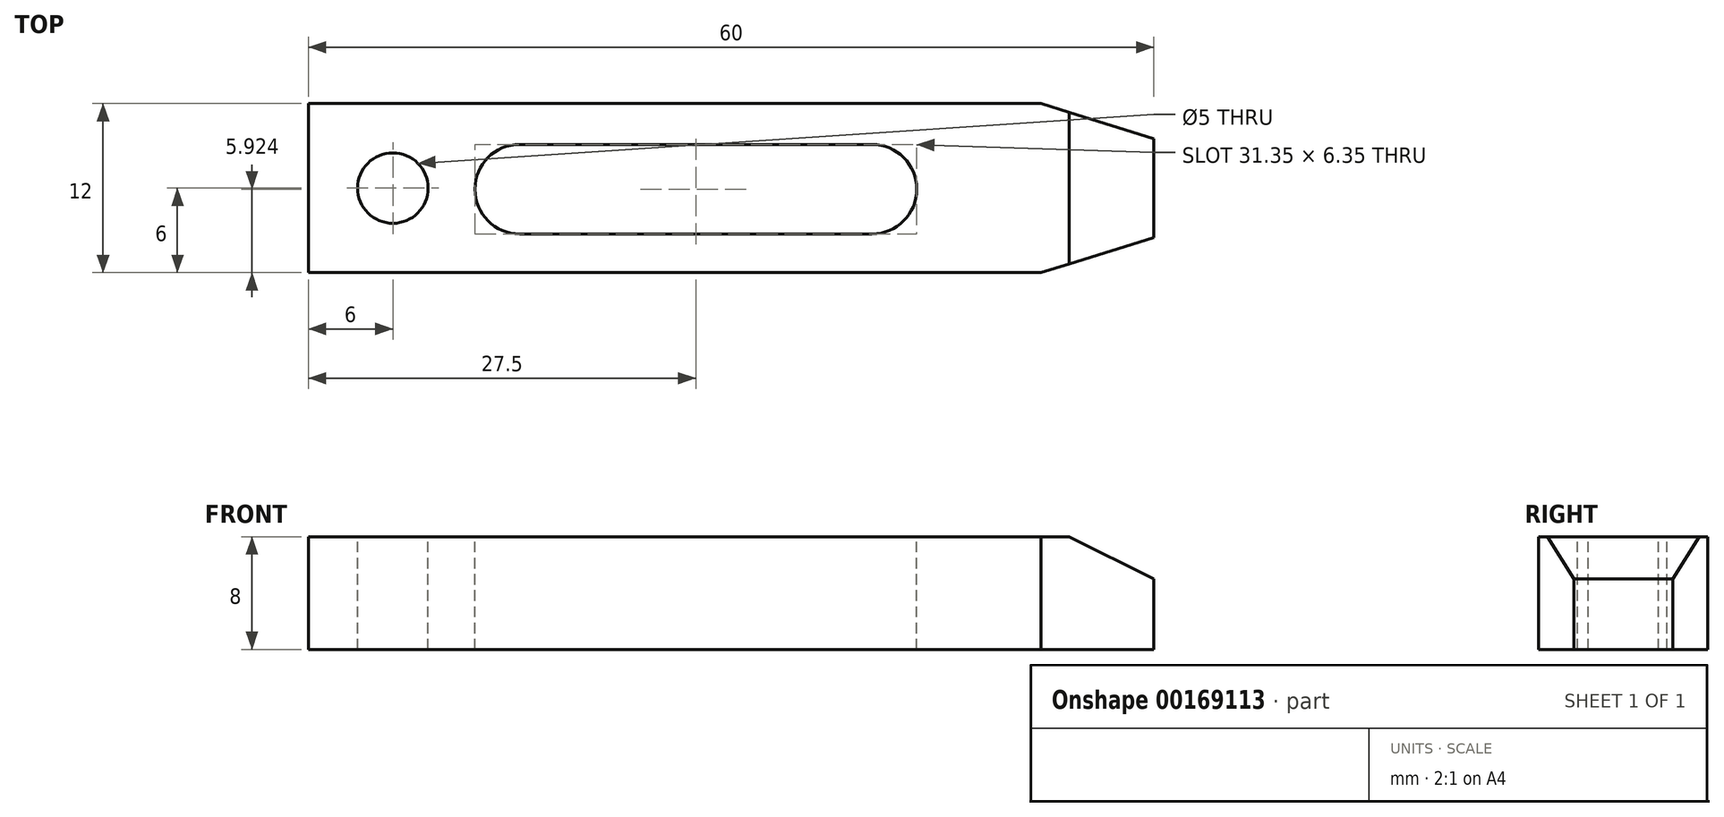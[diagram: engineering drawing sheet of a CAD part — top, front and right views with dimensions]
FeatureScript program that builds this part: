
annotation { "Feature Type Name" : "Feature", "Feature Type Description" : "" }
export const myFeature = defineFeature(function(context is Context, id is Id, definition is map)
    precondition{}
    {
        {
            var Q0;
            Q0=qCreatedBy(makeId("Top.planeOp"),FACE);
            var sketch = newSketch(context, id + "F0", { "sketchPlane" : qUnion([Q0])});
            skLineSegment(sketch, "E0.bottom", {"start": v(0, 0) * mm, "end": v(60, 0) * mm});
            skLineSegment(sketch, "E0.top", {"start": v(0, 12) * mm, "end": v(60, 12) * mm});
            skLineSegment(sketch, "E0.left", {"start": v(0, 0) * mm, "end": v(0, 12) * mm});
            skLineSegment(sketch, "E0.right", {"start": v(60, 0) * mm, "end": v(60, 12) * mm});
            skLineSegment(sketch, "E1", {"start": v(0, 6) * mm, "end": v(60, 6) * mm, "construction": true});
            skLineSegment(sketch, "E2", {"start": v(52, 12) * mm, "end": v(60, 9.5) * mm});
            skLineSegment(sketch, "E3.MirrorCS", {"start": v(52, 0) * mm, "end": v(60, 2.5) * mm});
            skSolve(sketch);
        }
        {
            var Q0;
            {var subQ3=sQuery(id+"F0.wireOp",EDGE,"E0.left");Q0=makeQuery(id+"F0.imprint","IMPRINT",FACE,{"disambiguationData":[TD([[makeQuery(id+"F0.imprint","IMPRINT",EDGE,{"derivedFrom":subQ3}),-1.0]])]});}
            extrude(context, id + "F1", {"entities" : qUnion([Q0]), "depth" : 8 * mm});
        }
        {
            var Q0;
            Q0=makeQuery(id+"F1.opExtrude","CAP_FACE",FACE,{"disambiguationData":[OSD([sQuery(id+"F0.wireOp",EDGE,"E0.bottom"),sQuery(id+"F0.wireOp",EDGE,"E0.top"),sQuery(id+"F0.wireOp",EDGE,"E0.left"),sQuery(id+"F0.wireOp",EDGE,"E0.right"),sQuery(id+"F0.wireOp",EDGE,"E2"),sQuery(id+"F0.wireOp",EDGE,"E3.MirrorCS")])],"isStart":false});
            var sketch = newSketch(context, id + "F2", { "sketchPlane" : qUnion([Q0])});
            skPoint(sketch, "E4", {"position": v(6, 6) * mm});
            skSolve(sketch);
        }
        {
            var Q0;
            Q0=sQuery(id+"F2.wireOp",VERTEX,"E4");
            var Q1;
            Q1=makeQuery(id+"F1.opExtrude","SWEPT_BODY",BODY,{"disambiguationData":[OSD([sQuery(id+"F0.wireOp",EDGE,"E0.bottom"),sQuery(id+"F0.wireOp",EDGE,"E0.top"),sQuery(id+"F0.wireOp",EDGE,"E0.left"),sQuery(id+"F0.wireOp",EDGE,"E0.right"),sQuery(id+"F0.wireOp",EDGE,"E2"),sQuery(id+"F0.wireOp",EDGE,"E3.MirrorCS")])]});
            hole(context, id + "F3", {"style" : HoleStyle.SIMPLE, "endStyle" : HoleEndStyle.THROUGH, "standardTappedOrClearance" : lookupTablePath({ "standard" : "ISO", "engagement" : "75%", "pitch" : "1 mm", "size" : "M6", "type" : "Tapped" }), "standardBlindInLast" : lookupTablePath({ "standard" : "ISO", "engagement" : "75%", "pitch" : "1 mm", "size" : "M6", "type" : "Tapped" }), "holeDiameter" : 5 * mm, "locations" : qUnion([Q0]), "scope" : qUnion([Q1]), "isTappedThrough" : true, "majorDiameter" : 6 * mm, "showTappedDepth" : true});
        }
        {
            var Q0;
            Q0=makeQuery(id+"F1.opExtrude","CAP_FACE",FACE,{"disambiguationData":[OSD([sQuery(id+"F0.wireOp",EDGE,"E0.bottom"),sQuery(id+"F0.wireOp",EDGE,"E0.top"),sQuery(id+"F0.wireOp",EDGE,"E0.left"),sQuery(id+"F0.wireOp",EDGE,"E0.right"),sQuery(id+"F0.wireOp",EDGE,"E2"),sQuery(id+"F0.wireOp",EDGE,"E3.MirrorCS")])],"isStart":false});
            var sketch = newSketch(context, id + "F4", { "sketchPlane" : qUnion([Q0])});
            skLineSegment(sketch, "E5", {"start": v(15, 5.92) * mm, "end": v(40, 5.92) * mm});
            skArc(sketch, "E6.0.startCap", {"start": v(15, 2.75) * mm, "mid": v(11.82, 5.92) * mm, "end": v(15, 9.1) * mm});
            skArc(sketch, "E6.0.endCap", {"start": v(40, 9.1) * mm, "mid": v(43.18, 5.92) * mm, "end": v(40, 2.75) * mm});
            skLineSegment(sketch, "E6.0.left", {"start": v(15, 9.1) * mm, "end": v(40, 9.1) * mm});
            skLineSegment(sketch, "E6.0.right", {"start": v(15, 2.75) * mm, "end": v(40, 2.75) * mm});
            skSolve(sketch);
        }
        {
            var Q0;
            Q0=qSketchRegion(id+"F4",true);
            extrude(context, id + "F5", {"entities" : qUnion([Q0]), "operationType" : NewBodyOperationType.REMOVE, "endBound" : BoundingType.THROUGH_ALL, "oppositeDirection" : true, "depth" : 25 * mm});
        }
        {
            var Q0;
            Q0=makeQuery(id+"F1.opExtrude","SWEPT_FACE",FACE,{"disambiguationData":[OSD([sQuery(id+"F0.wireOp",EDGE,"E0.bottom")])]});
            var sketch = newSketch(context, id + "F6", { "sketchPlane" : qUnion([Q0])});
            skLineSegment(sketch, "E7", {"start": v(54, 8) * mm, "end": v(60, 5) * mm});
            skLineSegment(sketch, "E8", {"start": v(60, 5) * mm, "end": v(60, 8) * mm});
            skLineSegment(sketch, "E9", {"start": v(60, 8) * mm, "end": v(54, 8) * mm});
            skSolve(sketch);
        }
        {
            var Q0;
            Q0=makeQuery(id+"F6.imprint","IMPRINT",FACE,{"disambiguationData":[TD([[makeQuery(id+"F6.imprint","IMPRINT",EDGE,{"derivedFrom":sQuery(id+"F6.wireOp",EDGE,"E7")}),1.0]])]});
            extrude(context, id + "F7", {"entities" : qUnion([Q0]), "operationType" : NewBodyOperationType.REMOVE, "endBound" : BoundingType.THROUGH_ALL, "oppositeDirection" : true, "depth" : 25 * mm});
        }
    });
